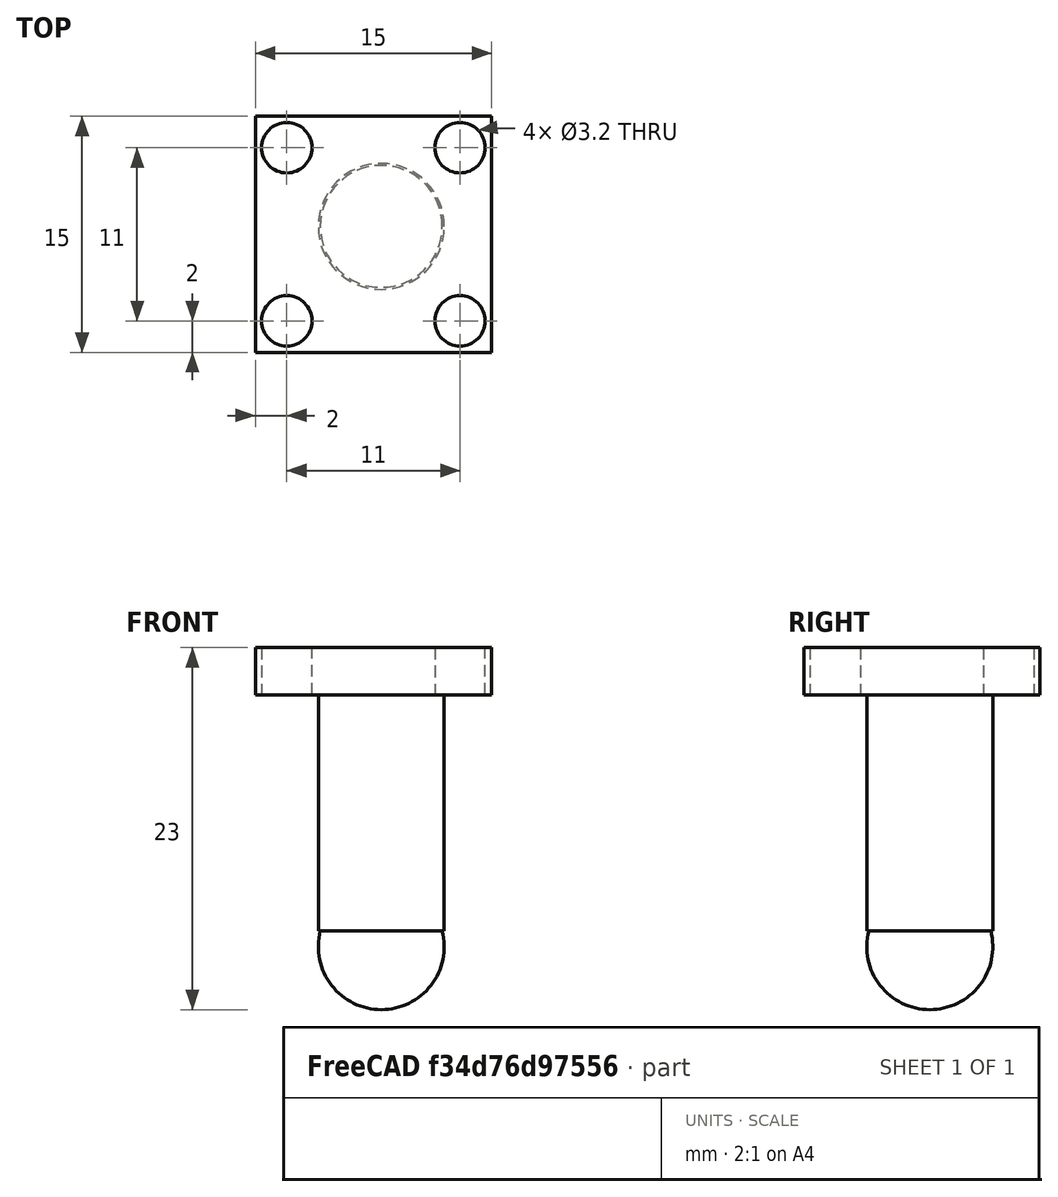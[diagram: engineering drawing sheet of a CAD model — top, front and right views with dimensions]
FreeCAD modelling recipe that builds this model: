
FCSTD DOCUMENT  (FreeCAD 0.21R33668 +26 (Git))
Label: ballcaster
License: All rights reserved
LicenseURL: https://en.wikipedia.org/wiki/All_rights_reserved
objects: Part::Cylinder×5, Part::MultiFuse×3, Part::Box×1, Part::Sphere×1, Part::Cut×1
note: 11 computed .brp shape members not serialized (recipe doc carries the construction recipe); baked Part::Feature solids carry a one-line shape summary decoded from their .brp

FEATURE [Part::Box] Box008  label="Cubo008"
  AttacherType = Attacher::AttachEngine3D
  Height = 3
  Length = 15
  Placement = pos=(-8,-8,4) rot=(0,0,1;0rad)
  Width = 15
FEATURE [Part::Cylinder] Cylinder011  label="Cilindro011"
  Angle = 360
  AttacherType = Attacher::AttachEngine3D
  FirstAngle = 0
  Height = 15
  Placement = pos=(0,0,-15) rot=(0,0,1;0rad)
  Radius = 4
  SecondAngle = 0
FEATURE [Part::Cylinder] Cylinder012  label="Cilindro012"
  Angle = 360
  AttacherType = Attacher::AttachEngine3D
  FirstAngle = 0
  Height = 10
  Placement = pos=(32,-6,-20) rot=(0,0,1;0rad)
  Radius = 1.6
  SecondAngle = 0
FEATURE [Part::Cylinder] Cylinder013  label="Cilindro013"
  Angle = 360
  AttacherType = Attacher::AttachEngine3D
  FirstAngle = 0
  Height = 10
  Placement = pos=(32,5,-20) rot=(0,0,1;0rad)
  Radius = 1.6
  SecondAngle = 0
FEATURE [Part::Cylinder] Cylinder014  label="Cilindro014"
  Angle = 360
  AttacherType = Attacher::AttachEngine3D
  FirstAngle = 0
  Height = 10
  Placement = pos=(21,-6,-20) rot=(0,0,1;0rad)
  Radius = 1.6
  SecondAngle = 0
FEATURE [Part::Cylinder] Cylinder015  label="Cilindro015"
  Angle = 360
  AttacherType = Attacher::AttachEngine3D
  FirstAngle = 0
  Height = 10
  Placement = pos=(21,5,-20) rot=(0,0,1;0rad)
  Radius = 1.6
  SecondAngle = 0
FEATURE [Part::MultiFuse] Fusion005
  Shapes = -> [Cylinder012,Cylinder013,Cylinder014,Cylinder015]
FEATURE [Part::Sphere] Sphere  label="Esfera"
  Angle1 = -90
  Angle2 = 90
  Angle3 = 360
  AttacherType = Attacher::AttachEngine3D
  Placement = pos=(0,0,-16) rot=(0,0,1;0rad)
  Radius = 4
FEATURE [Part::MultiFuse] Fusion010
  Placement = pos=(0,0,4) rot=(0,0,1;0rad)
  Shapes = -> [Cylinder011,Sphere]
FEATURE [Part::MultiFuse] Fusion011  label="ballcaster"
  Placement = pos=(27,0,-22) rot=(0,0,1;0rad)
  Shapes = -> [Fusion010,Box008]
FEATURE [Part::Cut] Cut009  label="ballCasterA"
  Base = -> Fusion011
  Placement = pos=(20,0,0) rot=(0,0,1;0rad)
  Tool = -> Fusion005
